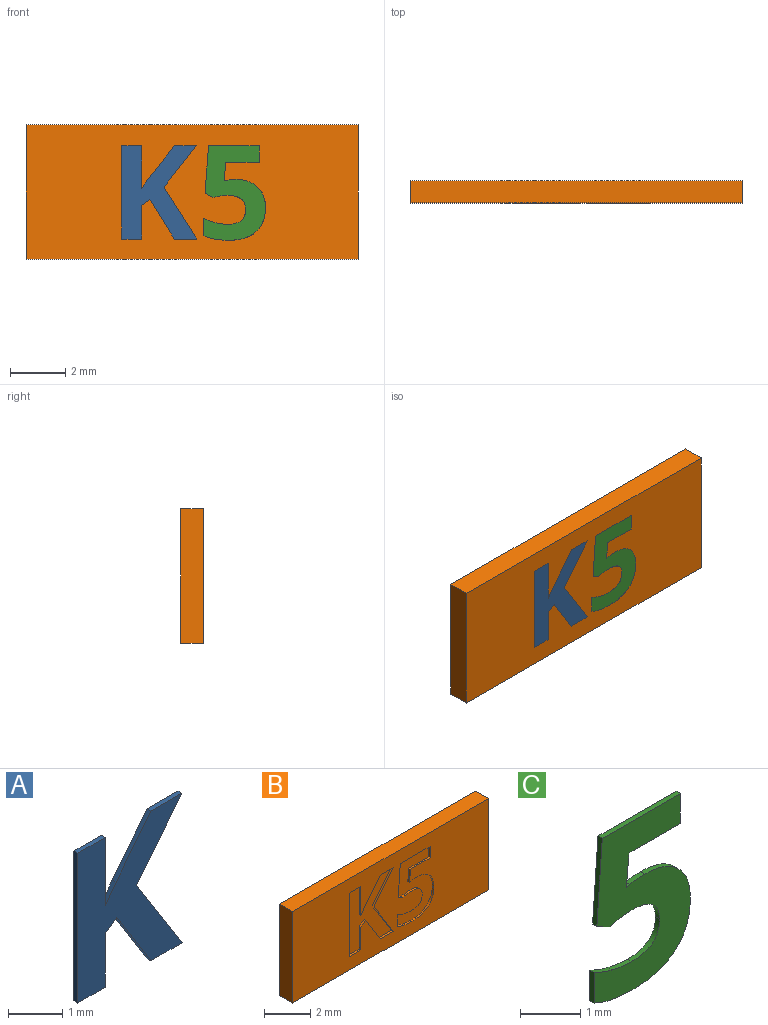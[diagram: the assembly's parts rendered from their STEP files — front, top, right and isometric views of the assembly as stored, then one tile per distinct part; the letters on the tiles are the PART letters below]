
ASSEMBLY  parts=3 mates=2
PART A: 15 faces, bbox 2.7x0.1x3.4 mm
  f0: plane 3.37x2.71mm, normal (0,-1,0), area 5.2mm2, adj f1,f2,f3,f4,f5,f6,f7,f8
  f1: plane 1.49x1.18mm, normal (0.79,0,-0.62), area 0.2mm2, adj f0,f2,f11,f13
  f2: plane 0.79x0.1mm, normal (0,0,1), area 0.1mm2, adj f0,f1,f3,f11
  f3: plane 1.15x0.91mm, normal (-0.78,0,0.62), area 0.1mm2, adj f0,f2,f4,f11
  f4: plane 0.4x0.28mm, normal (-0.82,0,0.58), area 0mm2, adj f0,f3,f5,f11
  f5: plane 1.54x0.1mm, normal (1,0,0), area 0.2mm2, adj f0,f4,f6,f11
  f6: plane 0.72x0.1mm, normal (0,0,1), area 0.1mm2, adj f0,f5,f7,f11
  f7: plane 3.37x0.1mm, normal (-1,0,0), area 0.3mm2, adj f0,f6,f8,f11
  f8: plane 0.72x0.1mm, normal (0,0,-1), area 0.1mm2, adj f0,f7,f9,f11
  f9: plane 1.2x0.1mm, normal (1,0,0), area 0.1mm2, adj f0,f8,f10,f11
  f10: plane 0.3x0.22mm, normal (0.58,0,-0.81), area 0mm2, adj f0,f9,f11,f12
  f11: plane 3.37x2.71mm, normal (0,1,0), area 5.2mm2, adj f1,f2,f3,f4,f5,f6,f7,f8
  f12: plane 1.42x0.88mm, normal (-0.85,0,-0.53), area 0.2mm2, adj f0,f10,f11,f14
  f13: plane 1.88x1.19mm, normal (0.85,0,0.53), area 0.2mm2, adj f0,f1,f11,f14
  f14: plane 0.81x0.1mm, normal (0,0,-1), area 0.1mm2, adj f0,f11,f12,f13
PART B: 41 faces, bbox 12x0.8x4.9 mm
  f0: plane 12x4.85mm, normal (0,-1,0), area 48.5mm2, adj f1,f2,f3,f4,f6,f7,f8,f9
  f1: plane 12x0.8mm, normal (0,0,-1), area 9.6mm2, adj f0,f2,f4,f5
  f2: plane 4.85x0.8mm, normal (1,0,0), area 3.9mm2, adj f0,f1,f3,f5
  f3: plane 12x0.8mm, normal (0,0,1), area 9.6mm2, adj f0,f2,f4,f5
  f4: plane 4.85x0.8mm, normal (-1,0,0), area 3.9mm2, adj f0,f1,f3,f5
  f5: plane 12x4.85mm, normal (0,1,0), area 58.2mm2, adj f1,f2,f3,f4
  f6: extruded ~0.35x0.1mm, area 0mm2, adj f0,f7,f25,f26
  f7: plane 0.1x0.08mm, normal (0.2,0,-0.98), area 0mm2, adj f0,f6,f8,f26
  f8: plane 0.66x0.1mm, normal (-1,0,0.09), area 0.1mm2, adj f0,f7,f9,f26
  f9: plane 1.2x0.1mm, normal (0,0,1), area 0.1mm2, adj f0,f8,f10,f26
  f10: plane 0.6x0.1mm, normal (-1,0,0), area 0.1mm2, adj f0,f9,f11,f26
  f11: plane 1.83x0.1mm, normal (0,0,-1), area 0.2mm2, adj f0,f10,f12,f26
  f12: plane 1.72x0.13mm, normal (1,0,-0.07), area 0.2mm2, adj f0,f11,f13,f26
  f13: plane 0.28x0.15mm, normal (0.47,0,0.88), area 0mm2, adj f0,f12,f14,f26
  f14: extruded ~0.24x0.1mm, area 0mm2, adj f0,f13,f15,f26
  f15: extruded ~0.27x0.1mm, area 0mm2, adj f0,f14,f16,f26
  f16: extruded ~0.68x0.51mm, area 0.1mm2, adj f0,f15,f17,f26
  f17: extruded ~0.65x0.54mm, area 0.1mm2, adj f0,f16,f18,f26
  f18: extruded ~0.46x0.1mm, area 0mm2, adj f0,f17,f19,f26
  f19: extruded ~0.42x0.16mm, area 0mm2, adj f0,f18,f20,f26
  f20: plane 0.62x0.1mm, normal (1,0,0), area 0.1mm2, adj f0,f19,f21,f26
  f21: extruded ~0.91x0.18mm, area 0.1mm2, adj f0,f20,f22,f26
  f22: extruded ~1x0.3mm, area 0.1mm2, adj f0,f21,f23,f26
  f23: extruded ~0.87x0.35mm, area 0.1mm2, adj f0,f22,f24,f26
  f24: extruded ~0.75x0.29mm, area 0.1mm2, adj f0,f23,f25,f26
  f25: extruded ~0.78x0.27mm, area 0.1mm2, adj f0,f6,f24,f26
  f26: plane 3.42x2.25mm, normal (0,-1,0), area 4.5mm2, adj f6,f7,f8,f9,f10,f11,f12,f13
  f27: plane 1.88x1.19mm, normal (-0.85,0,-0.53), area 0.2mm2, adj f0,f28,f39,f40
  f28: plane 1.49x1.18mm, normal (-0.79,0,0.62), area 0.2mm2, adj f0,f27,f29,f40
  f29: plane 0.79x0.1mm, normal (0,0,-1), area 0.1mm2, adj f0,f28,f30,f40
  f30: plane 1.15x0.91mm, normal (0.78,0,-0.62), area 0.1mm2, adj f0,f29,f31,f40
  f31: plane 0.4x0.28mm, normal (0.82,0,-0.58), area 0mm2, adj f0,f30,f32,f40
  f32: plane 1.54x0.1mm, normal (-1,0,0), area 0.2mm2, adj f0,f31,f33,f40
  f33: plane 0.72x0.1mm, normal (0,0,-1), area 0.1mm2, adj f0,f32,f34,f40
  f34: plane 3.37x0.1mm, normal (1,0,0), area 0.3mm2, adj f0,f33,f35,f40
  f35: plane 0.72x0.1mm, normal (0,0,1), area 0.1mm2, adj f0,f34,f36,f40
  f36: plane 1.2x0.1mm, normal (-1,0,0), area 0.1mm2, adj f0,f35,f37,f40
  f37: plane 0.3x0.22mm, normal (-0.58,0,0.81), area 0mm2, adj f0,f36,f38,f40
  f38: plane 1.42x0.88mm, normal (0.85,0,0.53), area 0.2mm2, adj f0,f37,f39,f40
  f39: plane 0.81x0.1mm, normal (0,0,1), area 0.1mm2, adj f0,f27,f38,f40
  f40: plane 3.37x2.71mm, normal (0,-1,0), area 5.2mm2, adj f27,f28,f29,f30,f31,f32,f33,f34
PART C: 22 faces, bbox 2.3x0.1x3.4 mm
  f0: plane 3.42x2.25mm, normal (0,-1,0), area 4.5mm2, adj f1,f2,f3,f4,f5,f6,f7,f8
  f1: plane 0.1x0.08mm, normal (-0.2,0,0.98), area 0mm2, adj f0,f2,f18,f20
  f2: plane 0.66x0.1mm, normal (1,0,-0.09), area 0.1mm2, adj f0,f1,f3,f18
  f3: plane 1.2x0.1mm, normal (0,0,-1), area 0.1mm2, adj f0,f2,f4,f18
  f4: plane 0.6x0.1mm, normal (1,0,0), area 0.1mm2, adj f0,f3,f5,f18
  f5: plane 1.83x0.1mm, normal (0,0,1), area 0.2mm2, adj f0,f4,f6,f18
  f6: plane 1.72x0.13mm, normal (-1,0,0.07), area 0.2mm2, adj f0,f5,f7,f18
  f7: plane 0.28x0.15mm, normal (-0.47,0,-0.88), area 0mm2, adj f0,f6,f8,f18
  f8: extruded ~0.24x0.1mm, area 0mm2, adj f0,f7,f9,f18
  f9: extruded ~0.27x0.1mm, area 0mm2, adj f0,f8,f10,f18
  f10: extruded ~0.68x0.51mm, area 0.1mm2, adj f0,f9,f11,f18
  f11: extruded ~0.65x0.54mm, area 0.1mm2, adj f0,f10,f12,f18
  f12: extruded ~0.46x0.1mm, area 0mm2, adj f0,f11,f13,f18
  f13: extruded ~0.42x0.16mm, area 0mm2, adj f0,f12,f14,f18
  f14: plane 0.62x0.1mm, normal (-1,0,0), area 0.1mm2, adj f0,f13,f15,f18
  f15: extruded ~0.91x0.18mm, area 0.1mm2, adj f0,f14,f16,f18
  f16: extruded ~1x0.3mm, area 0.1mm2, adj f0,f15,f17,f18
  f17: extruded ~0.87x0.35mm, area 0.1mm2, adj f0,f16,f18,f19
  f18: plane 3.42x2.25mm, normal (0,1,0), area 4.5mm2, adj f1,f2,f3,f4,f5,f6,f7,f8
  f19: extruded ~0.75x0.29mm, area 0.1mm2, adj f0,f17,f18,f21
  f20: extruded ~0.35x0.1mm, area 0mm2, adj f0,f1,f18,f21
  f21: extruded ~0.78x0.27mm, area 0.1mm2, adj f0,f18,f19,f20
PLACE A t=(-0.28,0.4,-0.03)mm
PLACE B t=(-0.01,0.4,-0.03)mm
PLACE C t=(-0.01,0.4,-0.03)mm
MATE fastened A.f0 <-> B.f0  axis (0,-1,0) through (-2.55,-0.4,-1.73)mm
MATE fastened C.f0 <-> B.f0  axis (0,-1,0) through (0.39,-0.4,-1.6)mm
